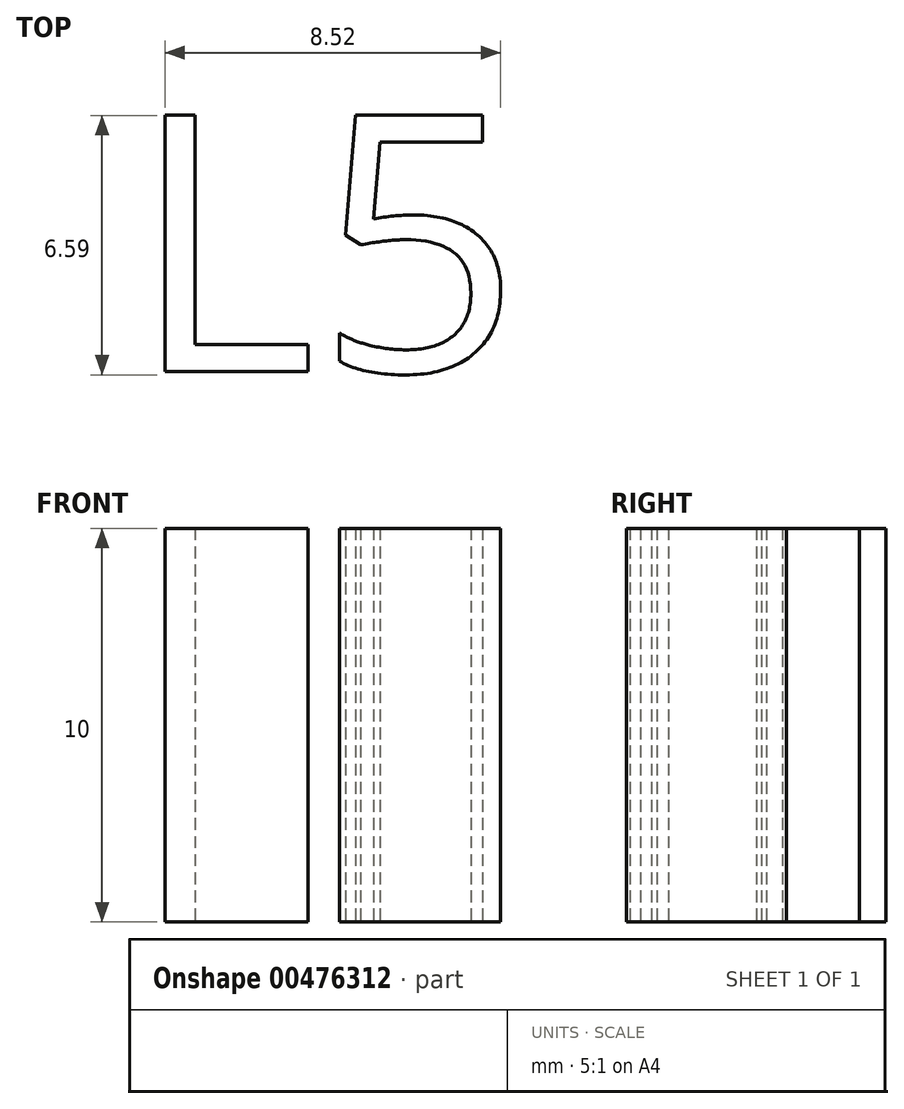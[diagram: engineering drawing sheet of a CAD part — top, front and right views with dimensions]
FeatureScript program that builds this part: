
annotation { "Feature Type Name" : "Feature", "Feature Type Description" : "" }
export const myFeature = defineFeature(function(context is Context, id is Id, definition is map)
    precondition{}
    {
        {
            var Q0;
            Q0=qCreatedBy(makeId("Top.planeOp"),FACE);
            var sketch = newSketch(context, id + "F0", { "sketchPlane" : qUnion([Q0])});
            skText(sketch, "E0", { "text": "L5", "fontName": "OpenSans-Regular.ttf"});
            skLineSegment(sketch, "E1", {"start": v(-5, 0) * mm, "end": v(5, 0) * mm, "construction": true});
            skLineSegment(sketch, "E2", {"start": v(0, 3.28) * mm, "end": v(0, -3.28) * mm});
            const initialGuessF0  = {"E0": [-0.005, -0.00328, 1, 0, 0.00656]};
            skSetInitialGuess(sketch, initialGuessF0);
            skSolve(sketch);
        }
        {
            var Q0;
            Q0 = qSketchRegion(id + "F0", true);
            extrude(context, id + "F1", {"entities" : qUnion([Q0]), "depth" : 10 * mm});
        }
    });
